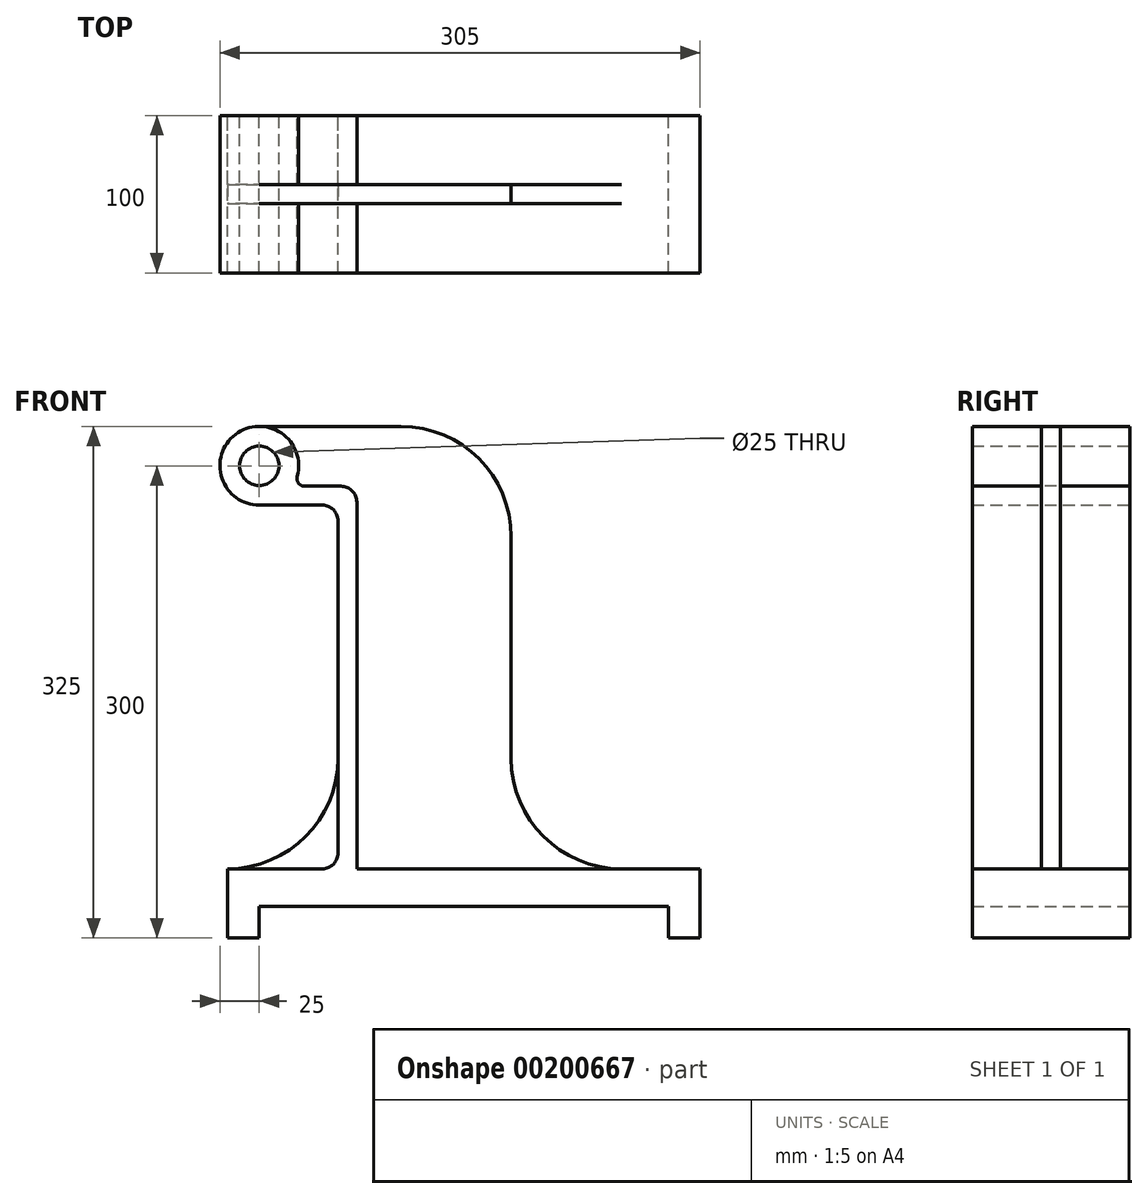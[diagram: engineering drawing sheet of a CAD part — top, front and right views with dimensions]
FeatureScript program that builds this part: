
annotation { "Feature Type Name" : "Feature", "Feature Type Description" : "" }
export const myFeature = defineFeature(function(context is Context, id is Id, definition is map)
    precondition{}
    {
        {
            var Q0;
            Q0=qCreatedBy(makeId("Front.planeOp"),FACE);
            var sketch = newSketch(context, id + "F0", { "sketchPlane" : qUnion([Q0])});
            skLineSegment(sketch, "E0", {"start": v(-150, -44) * mm, "end": v(-150, 0) * mm});
            skLineSegment(sketch, "E1", {"start": v(-150, 0) * mm, "end": v(150, 0) * mm});
            skLineSegment(sketch, "E2", {"start": v(150, 0) * mm, "end": v(150, -44) * mm});
            skLineSegment(sketch, "E3", {"start": v(150, -44) * mm, "end": v(130, -44) * mm});
            skLineSegment(sketch, "E4", {"start": v(130, -44) * mm, "end": v(130, -24) * mm});
            skLineSegment(sketch, "E5", {"start": v(130, -24) * mm, "end": v(-130, -24) * mm});
            skLineSegment(sketch, "E6", {"start": v(-130, -24) * mm, "end": v(-130, -44) * mm});
            skLineSegment(sketch, "E7", {"start": v(-130, -44) * mm, "end": v(-150, -44) * mm});
            skSolve(sketch);
        }
        {
            var Q0;
            Q0 = qSketchRegion(id + "F0", true);
            var Q1;
            Q1=makeQuery(id+"F0.imprint","IMPRINT",FACE,{"disambiguationData":[TD([[makeQuery(id+"F0.imprint","IMPRINT",EDGE,{"derivedFrom":sQuery(id+"F0.wireOp",EDGE,"E0")}),-1.0]])]});
            extrude(context, id + "F1", {"entities" : qUnion([Q0, Q1]), "depth" : 100 * mm});
        }
        {
            var Q0;
            Q0=qCreatedBy(makeId("Front.planeOp"),FACE);
            var sketch = newSketch(context, id + "F2", { "sketchPlane" : qUnion([Q0])});
            skLineSegment(sketch, "E8.0", {"start": v(130, -24) * mm, "end": v(-130, -24) * mm});
            skLineSegment(sketch, "E9.0", {"start": v(-150, 0) * mm, "end": v(150, 0) * mm});
            skCircle(sketch, "E10", {"center": v(-130, 256) * mm, "radius": 25 * mm});
            skCircle(sketch, "E11", {"center": v(-130, 256) * mm, "radius": 12.5 * mm});
            skLineSegment(sketch, "E12", {"start": v(-80, 0) * mm, "end": v(-80, 221) * mm});
            skLineSegment(sketch, "E13", {"start": v(-90, 231) * mm, "end": v(-130, 231) * mm});
            skPoint(sketch, "E14.visualSharp", {"position": v(-80, 231) * mm});
            skArc(sketch, "E14.filletArc", {"start": v(-80, 221) * mm, "mid": v(-82.93, 228.07) * mm, "end": v(-90, 231) * mm});
            skLineSegment(sketch, "E15", {"start": v(-68, 0) * mm, "end": v(-68, 233) * mm});
            skLineSegment(sketch, "E16", {"start": v(-78, 243) * mm, "end": v(-108.65, 243) * mm});
            skPoint(sketch, "E17.visualSharp", {"position": v(-68, 243) * mm});
            skArc(sketch, "E17.filletArc", {"start": v(-68, 233) * mm, "mid": v(-70.93, 240.07) * mm, "end": v(-78, 243) * mm});
            skSolve(sketch);
        }
        {
            var Q0;
            {var subQ1=sQuery(id+"F2.wireOp",EDGE,"E12");Q0=makeQuery(id+"F2.imprint","IMPRINT",FACE,{"disambiguationData":[TD([[makeQuery(id+"F2.imprint","IMPRINT",EDGE,{"derivedFrom":subQ1}),-1.0]])]});}
            var Q1;
            Q1=makeQuery(id+"F2.imprint","IMPRINT",FACE,{"disambiguationData":[TD([[makeQuery(id+"F2.imprint","IMPRINT",EDGE,{"derivedFrom":sQuery(id+"F2.wireOp",EDGE,"E11")}),-1.0]])]});
            extrude(context, id + "F3", {"entities" : qUnion([Q0, Q1]), "operationType" : NewBodyOperationType.ADD, "depth" : 100 * mm});
        }
        {
            var Q0;
            Q0=makeQuery(id+"F3.opExtrude","SWEPT_EDGE",EDGE,{"disambiguationData":[OSD([sQuery(id+"F2.wireOp",EDGE,"E10"),sQuery(id+"F2.wireOp",EDGE,"E16")])]});
            fillet(context, id + "F4", {"entities" : qUnion([Q0]), "radius" : 5 * mm, "tangentPropagation" : true, "allowEdgeOverflow" : false});
        }
        {
            var Q0;
            Q0=makeQuery(id+"F3.boolean.opBoolean","MERGE",FACE,{"derivedFrom":[makeQuery(id+"F1.opExtrude","CAP_FACE",FACE,{"disambiguationData":[OSD([sQuery(id+"F0.wireOp",EDGE,"E0"),sQuery(id+"F0.wireOp",EDGE,"E1"),sQuery(id+"F0.wireOp",EDGE,"E2"),sQuery(id+"F0.wireOp",EDGE,"E3"),sQuery(id+"F0.wireOp",EDGE,"E4"),sQuery(id+"F0.wireOp",EDGE,"E5"),sQuery(id+"F0.wireOp",EDGE,"E6"),sQuery(id+"F0.wireOp",EDGE,"E7")])],"isStart":true}),makeQuery(id+"F3.opExtrude","CAP_FACE",FACE,{"disambiguationData":[OSD([sQuery(id+"F2.wireOp",EDGE,"E9.0"),sQuery(id+"F2.wireOp",EDGE,"E10"),sQuery(id+"F2.wireOp",EDGE,"E11"),sQuery(id+"F2.wireOp",EDGE,"E12"),sQuery(id+"F2.wireOp",EDGE,"E13"),sQuery(id+"F2.wireOp",EDGE,"E14.filletArc"),sQuery(id+"F2.wireOp",EDGE,"E15"),sQuery(id+"F2.wireOp",EDGE,"E16"),sQuery(id+"F2.wireOp",EDGE,"E17.filletArc")])],"isStart":true})]});
            cPlane(context, id + "F5", {"entities" : qUnion([Q0]), "cplaneType" : CPlaneType.OFFSET, "offset" : 50 * mm, "oppositeDirection" : true, "width" : 150 * mm, "height" : 150 * mm});
        }
        {
            var Q0;
            Q0=qCreatedBy(id+"F5.planeOp",FACE);
            var sketch = newSketch(context, id + "F6", { "sketchPlane" : qUnion([Q0])});
            skLineSegment(sketch, "E18", {"start": v(132.94, 281) * mm, "end": v(40, 281) * mm});
            skLineSegment(sketch, "E19", {"start": v(-30, 211) * mm, "end": v(-30, 70) * mm});
            skPoint(sketch, "E20.visualSharp", {"position": v(-30, 281) * mm});
            skArc(sketch, "E20.filletArc", {"start": v(40, 281) * mm, "mid": v(-9.5, 260.5) * mm, "end": v(-30, 211) * mm});
            skPoint(sketch, "E21.newPointA", {"position": v(68, 0) * mm});
            skPoint(sketch, "E21.newPointB", {"position": v(-30, 0) * mm});
            skArc(sketch, "E21.filletArc", {"start": v(-100, 0) * mm, "mid": v(-50.5, 20.5) * mm, "end": v(-30, 70) * mm});
            skLineSegment(sketch, "E22.0", {"start": v(68, 0) * mm, "end": v(68, 233) * mm});
            skPoint(sketch, "E23.0", {"position": v(78, 243) * mm});
            skArc(sketch, "E24.0", {"start": v(68, 233) * mm, "mid": v(70.93, 240.07) * mm, "end": v(78, 243) * mm});
            skLineSegment(sketch, "E25.0", {"start": v(78, 243) * mm, "end": v(101.09, 243) * mm});
            skArc(sketch, "E26.0", {"start": v(105.9, 249.33) * mm, "mid": v(105.07, 244.97) * mm, "end": v(101.09, 243) * mm});
            skArc(sketch, "E27.0", {"start": v(105.9, 249.33) * mm, "mid": v(110.1, 271.14) * mm, "end": v(130, 281) * mm});
            skPoint(sketch, "E28.orphan", {"position": v(130, 231) * mm});
            skLineSegment(sketch, "E29.0", {"start": v(68, 0) * mm, "end": v(-100, 0) * mm});
            skPoint(sketch, "E30.0.end.orphan", {"position": v(-150, 0) * mm});
            skArc(sketch, "E31", {"start": v(80, 70) * mm, "mid": v(100.5, 20.5) * mm, "end": v(150, 0) * mm});
            skLineSegment(sketch, "E32.0", {"start": v(80, 0) * mm, "end": v(80, 221) * mm});
            skLineSegment(sketch, "E33.0", {"start": v(150, 0) * mm, "end": v(80, 0) * mm});
            skSolve(sketch);
        }
        {
            var Q0;
            Q0 = qSketchRegion(id + "F6", true);
            extrude(context, id + "F7", {"entities" : qUnion([Q0]), "operationType" : NewBodyOperationType.ADD, "endBound" : BoundingType.SYMMETRIC, "depth" : 12 * mm});
        }
        {
            var Q0;
            {var subQ0=sQuery(id+"F2.wireOp",EDGE,"E12");var subQ1=sQuery(id+"F2.wireOp",EDGE,"E9.0");Q0=makeQuery(id+"F7.boolean.opBoolean","SPLIT",EDGE,{"disambiguationData":[TD([makeQuery(id+"F7.opExtrude","CAP_FACE",FACE,{"disambiguationData":[OSD([sQuery(id+"F6.wireOp",EDGE,"E31"),sQuery(id+"F6.wireOp",EDGE,"E32.0"),sQuery(id+"F6.wireOp",EDGE,"E33.0")])],"isStart":true})])],"derivedFrom":makeQuery(id+"F3.opExtrude","SWEPT_EDGE",EDGE,{"disambiguationData":[OSD([subQ1,subQ0])]})});}
            var Q1;
            {var subQ0=sQuery(id+"F2.wireOp",EDGE,"E12");var subQ2=sQuery(id+"F2.wireOp",EDGE,"E9.0");Q1=makeQuery(id+"F7.boolean.opBoolean","SPLIT",EDGE,{"disambiguationData":[TD([makeQuery(id+"F7.opExtrude","CAP_FACE",FACE,{"disambiguationData":[OSD([sQuery(id+"F6.wireOp",EDGE,"E31"),sQuery(id+"F6.wireOp",EDGE,"E32.0"),sQuery(id+"F6.wireOp",EDGE,"E33.0")])],"isStart":false})])],"derivedFrom":makeQuery(id+"F3.opExtrude","SWEPT_EDGE",EDGE,{"disambiguationData":[OSD([subQ2,subQ0])]})});}
            var Q2;
            {var subQ0=sQuery(id+"F0.wireOp",EDGE,"E1");var subQ1=sQuery(id+"F2.wireOp",EDGE,"E15");var subQ2=sQuery(id+"F2.wireOp",EDGE,"E9.0");Q2=makeQuery(id+"F7.boolean.opBoolean","SPLIT",EDGE,{"disambiguationData":[TD([makeQuery(id+"F1.opExtrude","CAP_FACE",FACE,{"disambiguationData":[OSD([sQuery(id+"F0.wireOp",EDGE,"E0"),subQ0,sQuery(id+"F0.wireOp",EDGE,"E2"),sQuery(id+"F0.wireOp",EDGE,"E3"),sQuery(id+"F0.wireOp",EDGE,"E4"),sQuery(id+"F0.wireOp",EDGE,"E5"),sQuery(id+"F0.wireOp",EDGE,"E6"),sQuery(id+"F0.wireOp",EDGE,"E7")])],"isStart":true})])],"derivedFrom":makeQuery(id+"F3.opExtrude","SWEPT_EDGE",EDGE,{"disambiguationData":[OSD([subQ2,subQ1])]})});}
            var Q3;
            {var subQ0=sQuery(id+"F2.wireOp",EDGE,"E15");var subQ1=sQuery(id+"F2.wireOp",EDGE,"E9.0");var subQ2=sQuery(id+"F0.wireOp",EDGE,"E1");Q3=makeQuery(id+"F7.boolean.opBoolean","SPLIT",EDGE,{"disambiguationData":[TD([makeQuery(id+"F1.opExtrude","CAP_FACE",FACE,{"disambiguationData":[OSD([sQuery(id+"F0.wireOp",EDGE,"E0"),subQ2,sQuery(id+"F0.wireOp",EDGE,"E2"),sQuery(id+"F0.wireOp",EDGE,"E3"),sQuery(id+"F0.wireOp",EDGE,"E4"),sQuery(id+"F0.wireOp",EDGE,"E5"),sQuery(id+"F0.wireOp",EDGE,"E6"),sQuery(id+"F0.wireOp",EDGE,"E7")])],"isStart":false})])],"derivedFrom":makeQuery(id+"F3.opExtrude","SWEPT_EDGE",EDGE,{"disambiguationData":[OSD([subQ1,subQ0])]})});}
            fillet(context, id + "F8", {"entities" : qUnion([Q0, Q1, Q2, Q3]), "radius" : 10 * mm, "tangentPropagation" : true, "allowEdgeOverflow" : false});
        }
    });
